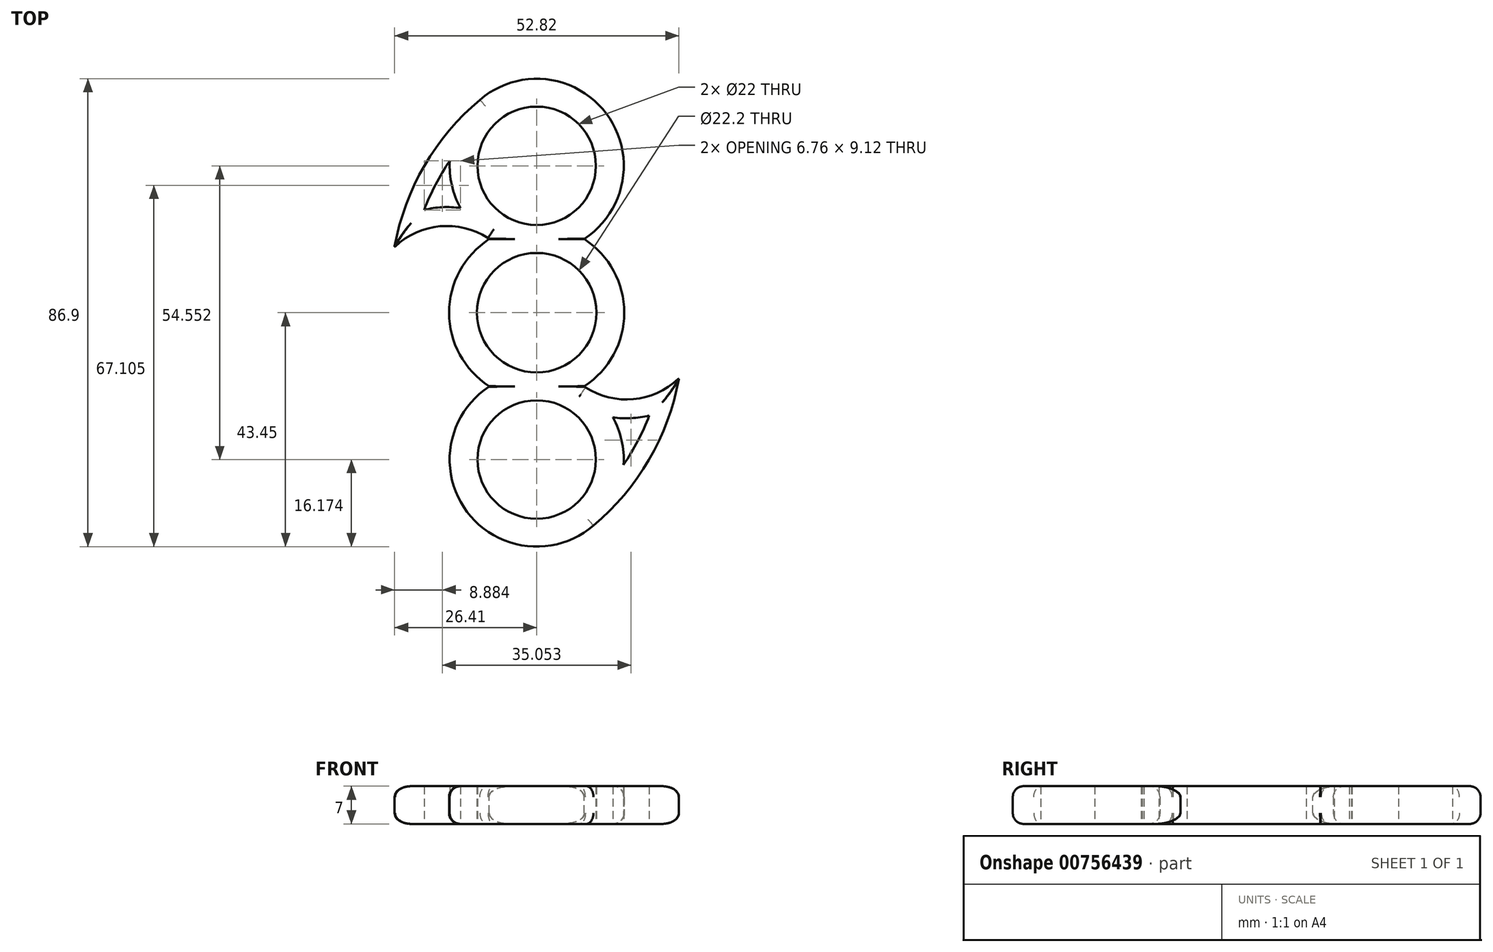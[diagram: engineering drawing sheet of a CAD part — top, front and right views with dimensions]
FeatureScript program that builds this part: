
annotation { "Feature Type Name" : "Feature", "Feature Type Description" : "" }
export const myFeature = defineFeature(function(context is Context, id is Id, definition is map)
    precondition{}
    {
        {
            var Q0;
            Q0=qCreatedBy(makeId("Top.planeOp"),FACE);
            var sketch = newSketch(context, id + "F0", { "sketchPlane" : qUnion([Q0])});
            skCircle(sketch, "E0", {"center": v(0, 0) * mm, "radius": 11.1 * mm});
            skCircle(sketch, "E1", {"center": v(0, 27.28) * mm, "radius": 11 * mm});
            skPoint(sketch, "E2.center", {"position": v(0, -0.22) * mm});
            skLineSegment(sketch, "E2.anchor1", {"start": v(0, -0.22) * mm, "end": v(0, 27.28) * mm, "construction": true});
            skLineSegment(sketch, "E2.anchor2", {"start": v(0, -0.22) * mm, "end": v(-18.53, -10.92) * mm, "construction": true});
            skCircle(sketch, "E3", {"center": v(0, 27.28) * mm, "radius": 16.18 * mm});
            skCircle(sketch, "E4", {"center": v(0, 0) * mm, "radius": 16.28 * mm});
            skCircle(sketch, "E5.1.0", {"center": v(0, -27.28) * mm, "radius": 16.18 * mm});
            skCircle(sketch, "E5.1.1", {"center": v(0, -27.28) * mm, "radius": 11 * mm});
            skArc(sketch, "E6", {"start": v(-10.06, 39.95) * mm, "mid": v(-20.73, 27.52) * mm, "end": v(-26.44, 12.17) * mm});
            skArc(sketch, "E7", {"start": v(-8.8, 13.7) * mm, "mid": v(-17.89, 16.06) * mm, "end": v(-26.44, 12.17) * mm});
            skArc(sketch, "E8.1.0", {"start": v(10.06, -39.95) * mm, "mid": v(20.73, -27.52) * mm, "end": v(26.44, -12.17) * mm});
            skArc(sketch, "E8.1.1", {"start": v(8.8, -13.7) * mm, "mid": v(17.89, -16.06) * mm, "end": v(26.44, -12.17) * mm});
            skArc(sketch, "E9.0", {"start": v(-14.15, 19.43) * mm, "mid": v(-17.54, 19.6) * mm, "end": v(-20.9, 19.1) * mm});
            skArc(sketch, "E9.1", {"start": v(-16.15, 28.21) * mm, "mid": v(-18.8, 23.8) * mm, "end": v(-20.9, 19.1) * mm});
            skArc(sketch, "E10.1.0", {"start": v(16.15, -28.21) * mm, "mid": v(18.8, -23.8) * mm, "end": v(20.9, -19.1) * mm});
            skArc(sketch, "E10.1.1", {"start": v(14.15, -19.43) * mm, "mid": v(17.54, -19.6) * mm, "end": v(20.9, -19.1) * mm});
            skSolve(sketch);
        }
        {
            var Q0;
            Q0=qSketchRegion(id+"F0",true);
            extrude(context, id + "F1", {"entities" : qUnion([Q0]), "depth" : 7 * mm, "offsetDistance" : 25.4 * mm});
        }
        {
            var Q0;
            {var subQ0=sQuery(id+"F0.wireOp",EDGE,"E6");var subQ1=sQuery(id+"F0.wireOp",EDGE,"E3");var subQ2=makeQuery(id+"F0.imprint","INTERSECT",VERTEX,{"disambiguationData":[OD(0.0)],"derivedFrom":[subQ1,subQ0]});Q0=makeQuery(id+"F1.opExtrude","CAP_EDGE",EDGE,{"disambiguationData":[OSD([subQ1]),TDD([makeQuery(id+"F0.imprint","IMPRINT",EDGE,{"disambiguationData":[TD([[subQ2,-1.0]])],"derivedFrom":subQ1}),makeQuery(id+"F0.imprint","IMPRINT",EDGE,{"disambiguationData":[TD([[subQ2,1.0]])],"derivedFrom":subQ1})])],"isStart":false});}
            var Q1;
            {var subQ0=sQuery(id+"F0.wireOp",EDGE,"E4");Q1=makeQuery(id+"F1.opExtrude","CAP_EDGE",EDGE,{"disambiguationData":[OSD([subQ0]),TDD([makeQuery(id+"F0.imprint","IMPRINT",EDGE,{"disambiguationData":[TD([[makeQuery(id+"F0.imprint","INTERSECT",VERTEX,{"derivedFrom":[subQ0,sQuery(id+"F0.wireOp",EDGE,"E5.1.0")]}),1.0]])],"derivedFrom":subQ0})])],"isStart":false});}
            var Q2;
            {var subQ0=sQuery(id+"F0.wireOp",EDGE,"E8.1.0");var subQ1=sQuery(id+"F0.wireOp",EDGE,"E5.1.0");var subQ2=makeQuery(id+"F0.imprint","INTERSECT",VERTEX,{"disambiguationData":[OD(0.0)],"derivedFrom":[subQ1,subQ0]});Q2=makeQuery(id+"F1.opExtrude","CAP_EDGE",EDGE,{"disambiguationData":[OSD([subQ1]),TDD([makeQuery(id+"F0.imprint","IMPRINT",EDGE,{"disambiguationData":[TD([[subQ2,-1.0]])],"derivedFrom":subQ1}),makeQuery(id+"F0.imprint","IMPRINT",EDGE,{"disambiguationData":[TD([[subQ2,1.0]])],"derivedFrom":subQ1})])],"isStart":false});}
            var Q3;
            Q3=makeQuery(id+"F1.opExtrude","CAP_EDGE",EDGE,{"disambiguationData":[OSD([sQuery(id+"F0.wireOp",EDGE,"E7")])],"isStart":false});
            var Q4;
            Q4=makeQuery(id+"F1.opExtrude","CAP_EDGE",EDGE,{"disambiguationData":[OSD([sQuery(id+"F0.wireOp",EDGE,"E8.1.1")])],"isStart":false});
            var Q5;
            {var subQ0=sQuery(id+"F0.wireOp",EDGE,"E4");Q5=makeQuery(id+"F1.opExtrude","CAP_EDGE",EDGE,{"disambiguationData":[OSD([subQ0]),TDD([makeQuery(id+"F0.imprint","IMPRINT",EDGE,{"disambiguationData":[TD([[makeQuery(id+"F0.imprint","INTERSECT",VERTEX,{"derivedFrom":[subQ0,sQuery(id+"F0.wireOp",EDGE,"E5.2.0")]}),1.0]])],"derivedFrom":subQ0})])],"isStart":false});}
            var Q6;
            {var subQ0=sQuery(id+"F0.wireOp",EDGE,"E8.2.0");var subQ1=sQuery(id+"F0.wireOp",EDGE,"E5.2.0");var subQ2=makeQuery(id+"F0.imprint","INTERSECT",VERTEX,{"disambiguationData":[OD(0.0)],"derivedFrom":[subQ1,subQ0]});Q6=makeQuery(id+"F1.opExtrude","CAP_EDGE",EDGE,{"disambiguationData":[OSD([subQ1]),TDD([makeQuery(id+"F0.imprint","IMPRINT",EDGE,{"disambiguationData":[TD([[subQ2,-1.0]])],"derivedFrom":subQ1}),makeQuery(id+"F0.imprint","IMPRINT",EDGE,{"disambiguationData":[TD([[subQ2,1.0]])],"derivedFrom":subQ1})])],"isStart":false});}
            var Q7;
            Q7=makeQuery(id+"F1.opExtrude","CAP_EDGE",EDGE,{"disambiguationData":[OSD([sQuery(id+"F0.wireOp",EDGE,"E8.2.0")])],"isStart":false});
            var Q8;
            Q8=makeQuery(id+"F1.opExtrude","CAP_EDGE",EDGE,{"disambiguationData":[OSD([sQuery(id+"F0.wireOp",EDGE,"E8.2.1")])],"isStart":false});
            var Q9;
            {var subQ0=sQuery(id+"F0.wireOp",EDGE,"E4");Q9=makeQuery(id+"F1.opExtrude","CAP_EDGE",EDGE,{"disambiguationData":[OSD([subQ0]),TDD([makeQuery(id+"F0.imprint","IMPRINT",EDGE,{"disambiguationData":[TD([[makeQuery(id+"F0.imprint","INTERSECT",VERTEX,{"derivedFrom":[sQuery(id+"F0.wireOp",EDGE,"E3"),subQ0]}),1.0]])],"derivedFrom":subQ0})])],"isStart":false});}
            var Q10;
            {var subQ0=sQuery(id+"F0.wireOp",EDGE,"E6");var subQ1=sQuery(id+"F0.wireOp",EDGE,"E3");var subQ2=makeQuery(id+"F0.imprint","INTERSECT",VERTEX,{"disambiguationData":[OD(0.0)],"derivedFrom":[subQ1,subQ0]});Q10=makeQuery(id+"F1.opExtrude","CAP_EDGE",EDGE,{"disambiguationData":[OSD([subQ1]),TDD([makeQuery(id+"F0.imprint","IMPRINT",EDGE,{"disambiguationData":[TD([[subQ2,-1.0]])],"derivedFrom":subQ1}),makeQuery(id+"F0.imprint","IMPRINT",EDGE,{"disambiguationData":[TD([[subQ2,1.0]])],"derivedFrom":subQ1})])],"isStart":true});}
            var Q11;
            Q11=makeQuery(id+"F1.opExtrude","CAP_EDGE",EDGE,{"disambiguationData":[OSD([sQuery(id+"F0.wireOp",EDGE,"E8.2.0")])],"isStart":true});
            var Q12;
            {var subQ0=sQuery(id+"F0.wireOp",EDGE,"E8.2.0");var subQ1=sQuery(id+"F0.wireOp",EDGE,"E5.2.0");var subQ2=makeQuery(id+"F0.imprint","INTERSECT",VERTEX,{"disambiguationData":[OD(0.0)],"derivedFrom":[subQ1,subQ0]});Q12=makeQuery(id+"F1.opExtrude","CAP_EDGE",EDGE,{"disambiguationData":[OSD([subQ1]),TDD([makeQuery(id+"F0.imprint","IMPRINT",EDGE,{"disambiguationData":[TD([[subQ2,-1.0]])],"derivedFrom":subQ1}),makeQuery(id+"F0.imprint","IMPRINT",EDGE,{"disambiguationData":[TD([[subQ2,1.0]])],"derivedFrom":subQ1})])],"isStart":true});}
            var Q13;
            {var subQ0=sQuery(id+"F0.wireOp",EDGE,"E4");Q13=makeQuery(id+"F1.opExtrude","CAP_EDGE",EDGE,{"disambiguationData":[OSD([subQ0]),TDD([makeQuery(id+"F0.imprint","IMPRINT",EDGE,{"disambiguationData":[TD([[makeQuery(id+"F0.imprint","INTERSECT",VERTEX,{"derivedFrom":[sQuery(id+"F0.wireOp",EDGE,"E3"),subQ0]}),1.0]])],"derivedFrom":subQ0})])],"isStart":true});}
            var Q14;
            Q14=makeQuery(id+"F1.opExtrude","CAP_EDGE",EDGE,{"disambiguationData":[OSD([sQuery(id+"F0.wireOp",EDGE,"E8.2.1")])],"isStart":true});
            var Q15;
            {var subQ0=sQuery(id+"F0.wireOp",EDGE,"E4");Q15=makeQuery(id+"F1.opExtrude","CAP_EDGE",EDGE,{"disambiguationData":[OSD([subQ0]),TDD([makeQuery(id+"F0.imprint","IMPRINT",EDGE,{"disambiguationData":[TD([[makeQuery(id+"F0.imprint","INTERSECT",VERTEX,{"derivedFrom":[subQ0,sQuery(id+"F0.wireOp",EDGE,"E5.2.0")]}),1.0]])],"derivedFrom":subQ0})])],"isStart":true});}
            var Q16;
            Q16=makeQuery(id+"F1.opExtrude","CAP_EDGE",EDGE,{"disambiguationData":[OSD([sQuery(id+"F0.wireOp",EDGE,"E8.1.1")])],"isStart":true});
            var Q17;
            Q17=makeQuery(id+"F1.opExtrude","CAP_EDGE",EDGE,{"disambiguationData":[OSD([sQuery(id+"F0.wireOp",EDGE,"E8.1.0")])],"isStart":true});
            var Q18;
            {var subQ0=sQuery(id+"F0.wireOp",EDGE,"E8.1.0");var subQ1=sQuery(id+"F0.wireOp",EDGE,"E5.1.0");var subQ2=makeQuery(id+"F0.imprint","INTERSECT",VERTEX,{"disambiguationData":[OD(0.0)],"derivedFrom":[subQ1,subQ0]});Q18=makeQuery(id+"F1.opExtrude","CAP_EDGE",EDGE,{"disambiguationData":[OSD([subQ1]),TDD([makeQuery(id+"F0.imprint","IMPRINT",EDGE,{"disambiguationData":[TD([[subQ2,-1.0]])],"derivedFrom":subQ1}),makeQuery(id+"F0.imprint","IMPRINT",EDGE,{"disambiguationData":[TD([[subQ2,1.0]])],"derivedFrom":subQ1})])],"isStart":true});}
            var Q19;
            {var subQ0=sQuery(id+"F0.wireOp",EDGE,"E4");Q19=makeQuery(id+"F1.opExtrude","CAP_EDGE",EDGE,{"disambiguationData":[OSD([subQ0]),TDD([makeQuery(id+"F0.imprint","IMPRINT",EDGE,{"disambiguationData":[TD([[makeQuery(id+"F0.imprint","INTERSECT",VERTEX,{"derivedFrom":[subQ0,sQuery(id+"F0.wireOp",EDGE,"E5.1.0")]}),1.0]])],"derivedFrom":subQ0})])],"isStart":true});}
            var Q20;
            Q20=makeQuery(id+"F1.opExtrude","CAP_EDGE",EDGE,{"disambiguationData":[OSD([sQuery(id+"F0.wireOp",EDGE,"E7")])],"isStart":true});
            fillet(context, id + "F2", {"entities" : qUnion([Q0, Q1, Q2, Q3, Q4, Q5, Q6, Q7, Q8, Q9, Q10, Q11, Q12, Q13, Q14, Q15, Q16, Q17, Q18, Q19, Q20]), "radius" : 2 * mm, "tangentPropagation" : true, "allowEdgeOverflow" : false});
        }
        {
            var Q0;
            {var subQ0=sQuery(id+"F0.wireOp",EDGE,"E7");var subQ1=sQuery(id+"F0.wireOp",EDGE,"E3");Q0=makeQuery(id+"F1.opExtrude","CAP_EDGE",EDGE,{"disambiguationData":[OSD([subQ1]),TDD([makeQuery(id+"F0.imprint","IMPRINT",EDGE,{"disambiguationData":[TD([[makeQuery(id+"F0.imprint","INTERSECT",VERTEX,{"derivedFrom":[subQ1,subQ0]}),-1.0]])],"derivedFrom":subQ1})])],"isStart":false});}
            var Q1;
            {var subQ0=sQuery(id+"F0.wireOp",EDGE,"E8.1.1");var subQ1=sQuery(id+"F0.wireOp",EDGE,"E5.1.0");Q1=makeQuery(id+"F1.opExtrude","CAP_EDGE",EDGE,{"disambiguationData":[OSD([subQ1]),TDD([makeQuery(id+"F0.imprint","IMPRINT",EDGE,{"disambiguationData":[TD([[makeQuery(id+"F0.imprint","INTERSECT",VERTEX,{"derivedFrom":[subQ1,subQ0]}),-1.0]])],"derivedFrom":subQ1})])],"isStart":false});}
            var Q2;
            {var subQ0=sQuery(id+"F0.wireOp",EDGE,"E8.1.1");var subQ1=sQuery(id+"F0.wireOp",EDGE,"E5.1.0");Q2=makeQuery(id+"F1.opExtrude","CAP_EDGE",EDGE,{"disambiguationData":[OSD([subQ1]),TDD([makeQuery(id+"F0.imprint","IMPRINT",EDGE,{"disambiguationData":[TD([[makeQuery(id+"F0.imprint","INTERSECT",VERTEX,{"derivedFrom":[subQ1,subQ0]}),-1.0]])],"derivedFrom":subQ1})])],"isStart":true});}
            var Q3;
            {var subQ0=sQuery(id+"F0.wireOp",EDGE,"E7");var subQ1=sQuery(id+"F0.wireOp",EDGE,"E3");Q3=makeQuery(id+"F1.opExtrude","CAP_EDGE",EDGE,{"disambiguationData":[OSD([subQ1]),TDD([makeQuery(id+"F0.imprint","IMPRINT",EDGE,{"disambiguationData":[TD([[makeQuery(id+"F0.imprint","INTERSECT",VERTEX,{"derivedFrom":[subQ1,subQ0]}),-1.0]])],"derivedFrom":subQ1})])],"isStart":true});}
            fillet(context, id + "F3", {"entities" : qUnion([Q0, Q1, Q2, Q3]), "radius" : 2 * mm, "tangentPropagation" : true, "allowEdgeOverflow" : false});
        }
        {
            var Q0;
            Q0=makeQuery(id+"F1.opExtrude","SWEPT_FACE",FACE,{"disambiguationData":[OSD([sQuery(id+"F0.wireOp",EDGE,"E8.1.0")])]});
            var Q1;
            {var subQ0=sQuery(id+"F0.wireOp",EDGE,"E8.1.0");var subQ1=sQuery(id+"F0.wireOp",EDGE,"E5.1.0");var subQ2=makeQuery(id+"F0.imprint","INTERSECT",VERTEX,{"disambiguationData":[OD(0.0)],"derivedFrom":[subQ1,subQ0]});Q1=makeQuery(id+"F1.opExtrude","SWEPT_FACE",FACE,{"disambiguationData":[OSD([subQ1]),TDD([makeQuery(id+"F0.imprint","IMPRINT",EDGE,{"disambiguationData":[TD([[subQ2,-1.0]])],"derivedFrom":subQ1}),makeQuery(id+"F0.imprint","IMPRINT",EDGE,{"disambiguationData":[TD([[subQ2,1.0]])],"derivedFrom":subQ1})])]});}
            var Q2;
            {var subQ0=sQuery(id+"F0.wireOp",EDGE,"E4");Q2=makeQuery(id+"F1.opExtrude","SWEPT_FACE",FACE,{"disambiguationData":[OSD([subQ0]),TDD([makeQuery(id+"F0.imprint","IMPRINT",EDGE,{"disambiguationData":[TD([[makeQuery(id+"F0.imprint","INTERSECT",VERTEX,{"derivedFrom":[subQ0,sQuery(id+"F0.wireOp",EDGE,"E5.2.0")]}),1.0]])],"derivedFrom":subQ0})])]});}
            var Q3;
            Q3=makeQuery(id+"F1.opExtrude","SWEPT_FACE",FACE,{"disambiguationData":[OSD([sQuery(id+"F0.wireOp",EDGE,"E8.1.1")])]});
            var Q4;
            {var subQ0=sQuery(id+"F0.wireOp",EDGE,"E8.2.0");var subQ1=sQuery(id+"F0.wireOp",EDGE,"E5.2.0");var subQ2=makeQuery(id+"F0.imprint","INTERSECT",VERTEX,{"disambiguationData":[OD(0.0)],"derivedFrom":[subQ1,subQ0]});Q4=makeQuery(id+"F1.opExtrude","SWEPT_FACE",FACE,{"disambiguationData":[OSD([subQ1]),TDD([makeQuery(id+"F0.imprint","IMPRINT",EDGE,{"disambiguationData":[TD([[subQ2,-1.0]])],"derivedFrom":subQ1}),makeQuery(id+"F0.imprint","IMPRINT",EDGE,{"disambiguationData":[TD([[subQ2,1.0]])],"derivedFrom":subQ1})])]});}
            var Q5;
            Q5=makeQuery(id+"F1.opExtrude","SWEPT_FACE",FACE,{"disambiguationData":[OSD([sQuery(id+"F0.wireOp",EDGE,"E8.2.0")])]});
            var Q6;
            {var subQ0=sQuery(id+"F0.wireOp",EDGE,"E6");var subQ1=sQuery(id+"F0.wireOp",EDGE,"E3");var subQ2=makeQuery(id+"F0.imprint","INTERSECT",VERTEX,{"disambiguationData":[OD(0.0)],"derivedFrom":[subQ1,subQ0]});Q6=makeQuery(id+"F1.opExtrude","SWEPT_FACE",FACE,{"disambiguationData":[OSD([subQ1]),TDD([makeQuery(id+"F0.imprint","IMPRINT",EDGE,{"disambiguationData":[TD([[subQ2,-1.0]])],"derivedFrom":subQ1}),makeQuery(id+"F0.imprint","IMPRINT",EDGE,{"disambiguationData":[TD([[subQ2,1.0]])],"derivedFrom":subQ1})])]});}
            var Q7;
            Q7=makeQuery(id+"F1.opExtrude","SWEPT_FACE",FACE,{"disambiguationData":[OSD([sQuery(id+"F0.wireOp",EDGE,"E8.2.1")])]});
            var Q8;
            Q8=makeQuery(id+"F1.opExtrude","SWEPT_FACE",FACE,{"disambiguationData":[OSD([sQuery(id+"F0.wireOp",EDGE,"E6")])]});
            var Q9;
            {var subQ0=sQuery(id+"F0.wireOp",EDGE,"E4");Q9=makeQuery(id+"F1.opExtrude","SWEPT_FACE",FACE,{"disambiguationData":[OSD([subQ0]),TDD([makeQuery(id+"F0.imprint","IMPRINT",EDGE,{"disambiguationData":[TD([[makeQuery(id+"F0.imprint","INTERSECT",VERTEX,{"derivedFrom":[sQuery(id+"F0.wireOp",EDGE,"E3"),subQ0]}),1.0]])],"derivedFrom":subQ0})])]});}
            var Q10;
            {var subQ0=sQuery(id+"F0.wireOp",EDGE,"E4");Q10=makeQuery(id+"F1.opExtrude","SWEPT_FACE",FACE,{"disambiguationData":[OSD([subQ0]),TDD([makeQuery(id+"F0.imprint","IMPRINT",EDGE,{"disambiguationData":[TD([[makeQuery(id+"F0.imprint","INTERSECT",VERTEX,{"derivedFrom":[subQ0,sQuery(id+"F0.wireOp",EDGE,"E5.1.0")]}),1.0]])],"derivedFrom":subQ0})])]});}
            var Q11;
            Q11=makeQuery(id+"F1.opExtrude","SWEPT_FACE",FACE,{"disambiguationData":[OSD([sQuery(id+"F0.wireOp",EDGE,"E7")])]});
            fillet(context, id + "F4", {"entities" : qUnion([Q0, Q1, Q2, Q3, Q4, Q5, Q6, Q7, Q8, Q9, Q10, Q11]), "radius" : 0.06 * mm, "tangentPropagation" : true, "allowEdgeOverflow" : false});
        }
    });
